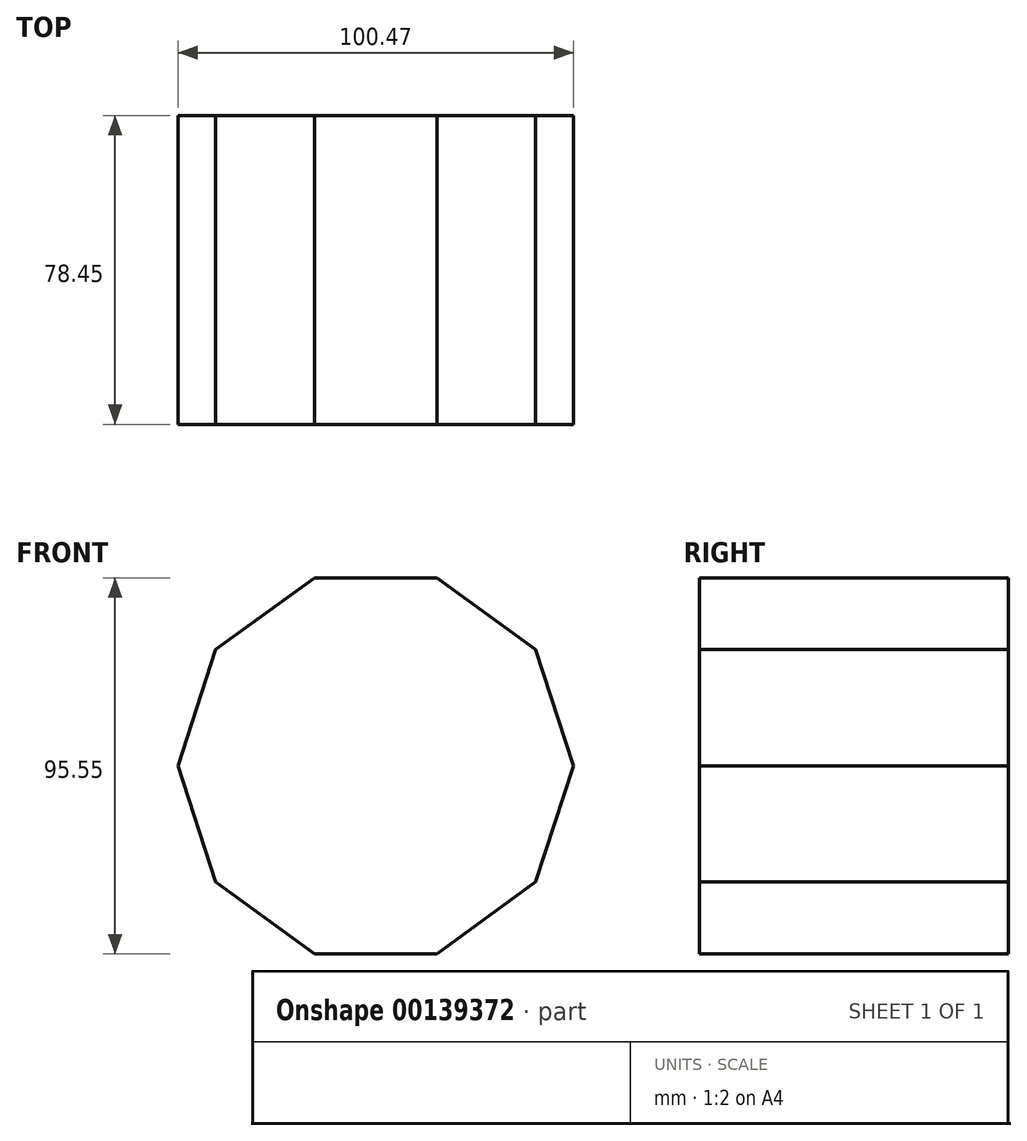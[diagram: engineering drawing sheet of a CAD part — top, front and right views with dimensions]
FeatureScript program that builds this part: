
annotation { "Feature Type Name" : "Feature", "Feature Type Description" : "" }
export const myFeature = defineFeature(function(context is Context, id is Id, definition is map)
    precondition{}
    {
        {
            var Q0;
            Q0=qCreatedBy(makeId("Front.planeOp"),FACE);
            var sketch = newSketch(context, id + "F0", { "sketchPlane" : qUnion([Q0])});
            skCircle(sketch, "E0.cCircle", {"center": v(-60, 47.78) * mm, "radius": 47.78 * mm, "construction": true});
            skLineSegment(sketch, "E0.0", {"start": v(-44.48, 0) * mm, "end": v(-75.53, 0) * mm});
            skLineSegment(sketch, "E0.1", {"start": v(-75.53, 0) * mm, "end": v(-100.65, 18.25) * mm});
            skLineSegment(sketch, "E0.2", {"start": v(-100.65, 18.25) * mm, "end": v(-110.24, 47.78) * mm});
            skLineSegment(sketch, "E0.3", {"start": v(-110.24, 47.78) * mm, "end": v(-100.65, 77.3) * mm});
            skLineSegment(sketch, "E0.4", {"start": v(-100.65, 77.3) * mm, "end": v(-75.53, 95.55) * mm});
            skLineSegment(sketch, "E0.5", {"start": v(-75.53, 95.55) * mm, "end": v(-44.48, 95.55) * mm});
            skLineSegment(sketch, "E0.6", {"start": v(-44.48, 95.55) * mm, "end": v(-19.37, 77.3) * mm});
            skLineSegment(sketch, "E0.7", {"start": v(-19.37, 77.3) * mm, "end": v(-9.77, 47.78) * mm});
            skLineSegment(sketch, "E0.8", {"start": v(-9.77, 47.78) * mm, "end": v(-19.37, 18.25) * mm});
            skLineSegment(sketch, "E0.9", {"start": v(-19.37, 18.25) * mm, "end": v(-44.48, 0) * mm});
            skPoint(sketch, "E0.0.midPoint", {"position": v(-60, 0) * mm});
            skSolve(sketch);
        }
        {
            var Q0;
            Q0 = qSketchRegion(id + "F0", true);
            extrude(context, id + "F1", {"entities" : qUnion([Q0]), "oppositeDirection" : true, "depth" : 78.45 * mm});
        }
    });
